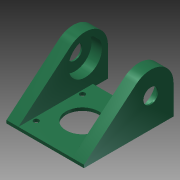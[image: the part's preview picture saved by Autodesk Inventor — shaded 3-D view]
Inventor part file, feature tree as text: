
AUTODESK INVENTOR PART (.ipt)
format: ipt  version: 2015 (Build 190159000, 159)  size: 159,744 bytes
history: native  units: mm
features: extrude x3, sketch x2, mirror x1, projected_geometry x1
ambient origin geometry x8: Origin, YZ Plane, XZ Plane, XY Plane, X Axis, Y Axis, Z Axis, Center Point
bodies: Solid1 (feature_tree)
feature tree (7):
  extrude  "Extrusion1"  Depth=31.0mm
  sketch  "Sketch2"  dims[d2=31.0mm d3=3.5mm d4=50.0mm d5=50.0mm d6=2.0mm d7=0.0mm d8=19.85mm d9=19.583mm d10=10.0mm d11=22.5mm d12=2.0mm d13=2.0mm d14=7.0mm d15=0.0mm d16=1.0mm d17=0.0mm]
  extrude  "Extrusion2"  Depth=1.0mm
  extrude  "Extrusion3"  Depth=50.0mm
  mirror  "Mirror1"
  sketch  "Sketch1"  dims[d0=22.1mm d1=31.0mm]
  projected_geometry  "Projected Loop1"
